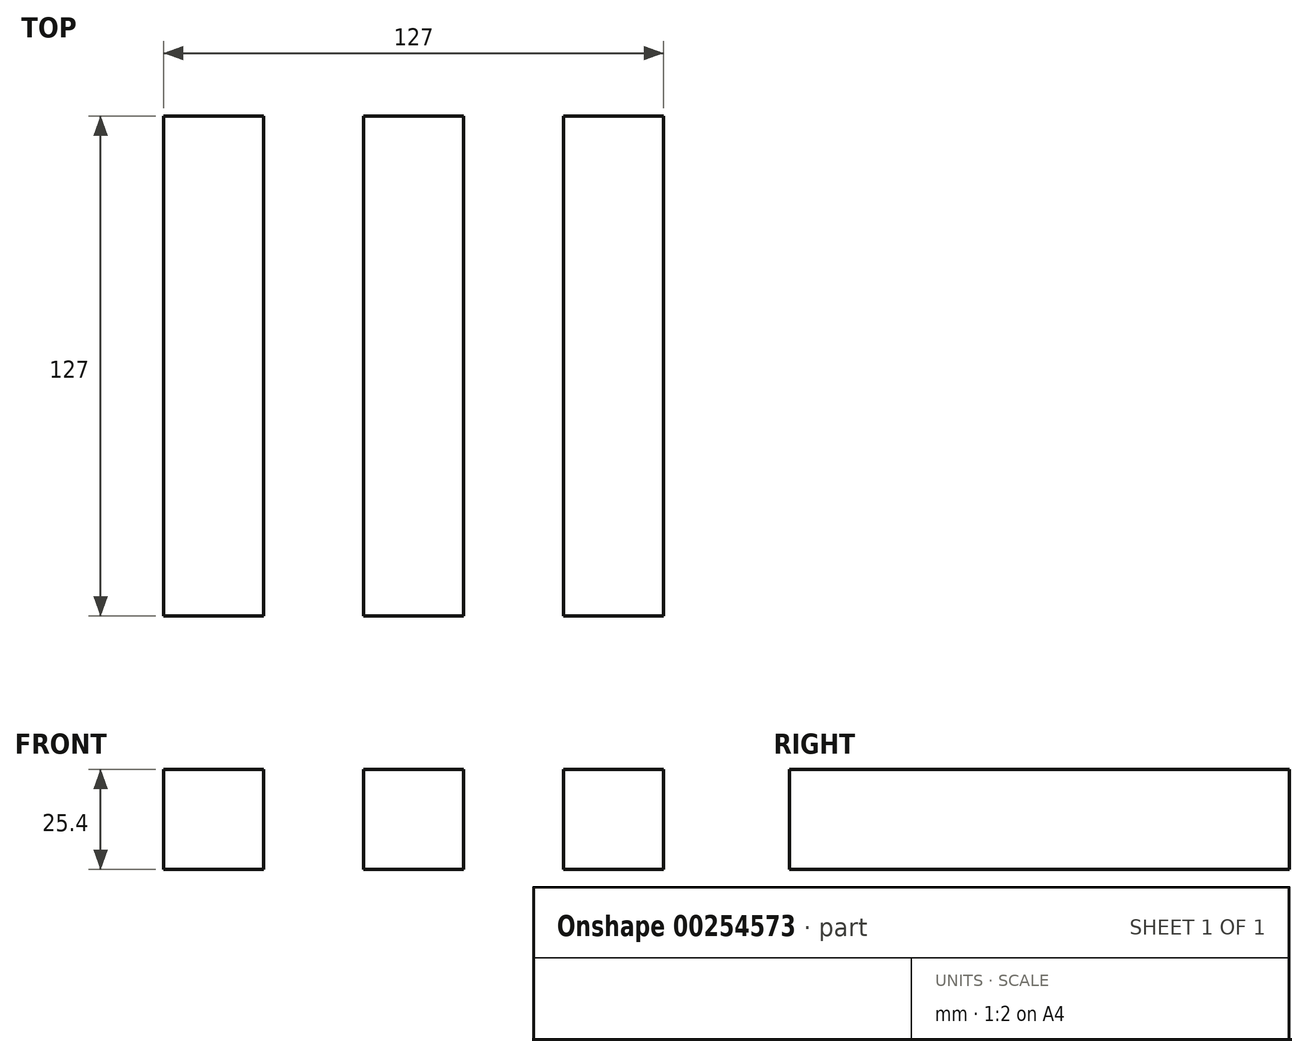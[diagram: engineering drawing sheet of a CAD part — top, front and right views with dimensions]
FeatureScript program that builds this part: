
annotation { "Feature Type Name" : "Feature", "Feature Type Description" : "" }
export const myFeature = defineFeature(function(context is Context, id is Id, definition is map)
    precondition{}
    {
        {
            var Q0;
            Q0=qCreatedBy(makeId("Front.planeOp"),FACE);
            var sketch = newSketch(context, id + "F0", { "sketchPlane" : qUnion([Q0])});
            skLineSegment(sketch, "E0", {"start": v(0, 0) * mm, "end": v(-50.8, 0) * mm});
            skLineSegment(sketch, "E1", {"start": v(-50.8, 0) * mm, "end": v(0, 0) * mm});
            skLineSegment(sketch, "E2", {"start": v(0, 0) * mm, "end": v(50.8, 0) * mm});
            skLineSegment(sketch, "E3.bottom", {"start": v(12.7, 12.7) * mm, "end": v(-12.7, 12.7) * mm});
            skLineSegment(sketch, "E3.top", {"start": v(12.7, -12.7) * mm, "end": v(-12.7, -12.7) * mm});
            skLineSegment(sketch, "E3.left", {"start": v(12.7, 12.7) * mm, "end": v(12.7, -12.7) * mm});
            skLineSegment(sketch, "E3.right", {"start": v(-12.7, 12.7) * mm, "end": v(-12.7, -12.7) * mm});
            skPoint(sketch, "E3.middle", {"position": v(0, 0) * mm});
            skLineSegment(sketch, "E4.bottom", {"start": v(63.5, 12.7) * mm, "end": v(38.1, 12.7) * mm});
            skLineSegment(sketch, "E4.top", {"start": v(63.5, -12.7) * mm, "end": v(38.1, -12.7) * mm});
            skLineSegment(sketch, "E4.left", {"start": v(63.5, 12.7) * mm, "end": v(63.5, -12.7) * mm});
            skLineSegment(sketch, "E4.right", {"start": v(38.1, 12.7) * mm, "end": v(38.1, -12.7) * mm});
            skPoint(sketch, "E4.middle", {"position": v(50.8, 0) * mm});
            skLineSegment(sketch, "E5.bottom", {"start": v(-38.1, 12.7) * mm, "end": v(-63.5, 12.7) * mm});
            skLineSegment(sketch, "E5.top", {"start": v(-38.1, -12.7) * mm, "end": v(-63.5, -12.7) * mm});
            skLineSegment(sketch, "E5.left", {"start": v(-38.1, 12.7) * mm, "end": v(-38.1, -12.7) * mm});
            skLineSegment(sketch, "E5.right", {"start": v(-63.5, 12.7) * mm, "end": v(-63.5, -12.7) * mm});
            skPoint(sketch, "E5.middle", {"position": v(-50.8, 0) * mm});
            skSolve(sketch);
        }
        {
            var Q0;
            {var subQ3=sQuery(id+"F0.wireOp",EDGE,"E5.bottom");Q0=makeQuery(id+"F0.imprint","IMPRINT",FACE,{"disambiguationData":[TD([[makeQuery(id+"F0.imprint","IMPRINT",EDGE,{"derivedFrom":subQ3}),1.0]])]});}
            var Q1;
            {var subQ1=sQuery(id+"F0.wireOp",EDGE,"E3.bottom");Q1=makeQuery(id+"F0.imprint","IMPRINT",FACE,{"disambiguationData":[TD([[makeQuery(id+"F0.imprint","IMPRINT",EDGE,{"derivedFrom":subQ1}),1.0]])]});}
            var Q2;
            {var subQ1=sQuery(id+"F0.wireOp",EDGE,"E3.top");Q2=makeQuery(id+"F0.imprint","IMPRINT",FACE,{"disambiguationData":[TD([[makeQuery(id+"F0.imprint","IMPRINT",EDGE,{"derivedFrom":subQ1}),-1.0]])]});}
            var Q3;
            {var subQ1=sQuery(id+"F0.wireOp",EDGE,"E4.bottom");Q3=makeQuery(id+"F0.imprint","IMPRINT",FACE,{"disambiguationData":[TD([[makeQuery(id+"F0.imprint","IMPRINT",EDGE,{"derivedFrom":subQ1}),1.0]])]});}
            extrude(context, id + "F1", {"entities" : qUnion([Q0, Q1, Q2, Q3]), "endBound" : BoundingType.SYMMETRIC, "depth" : 127 * mm});
        }
    });
